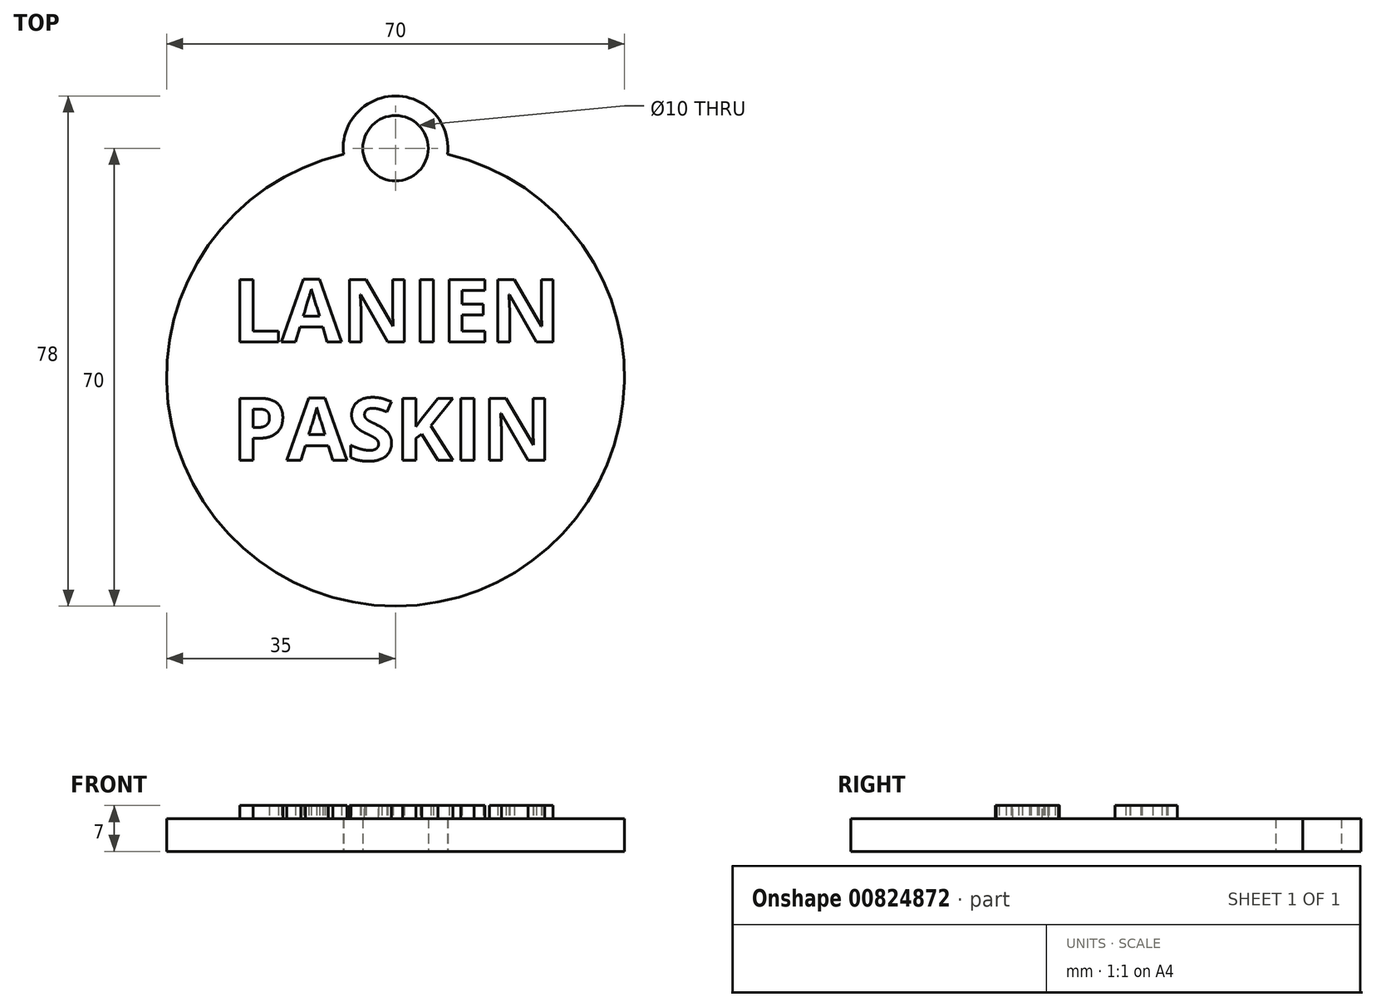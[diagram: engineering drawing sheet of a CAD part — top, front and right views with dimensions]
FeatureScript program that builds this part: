
annotation { "Feature Type Name" : "Feature", "Feature Type Description" : "" }
export const myFeature = defineFeature(function(context is Context, id is Id, definition is map)
    precondition{}
    {
        {
            var Q0;
            Q0=qCreatedBy(makeId("Top.planeOp"),FACE);
            var sketch = newSketch(context, id + "F0", { "sketchPlane" : qUnion([Q0])});
            skCircle(sketch, "E0", {"center": v(-60, 0) * mm, "radius": 35 * mm});
            skText(sketch, "E1", { "text": "LANIEN \nPASKIN", "fontName": "OpenSans-Bold.ttf"});
            skCircle(sketch, "E2", {"center": v(-60, 35) * mm, "radius": 5 * mm});
            skCircle(sketch, "E3.0", {"center": v(-60, 35) * mm, "radius": 8 * mm});
            skText(sketch, "E4", { "text": "SULO\nKUSI\n", "fontName": "OpenSans-Bold.ttf"});
            skCircle(sketch, "E5", {"center": v(60, 35) * mm, "radius": 5 * mm});
            skCircle(sketch, "E6.0", {"center": v(60, 35) * mm, "radius": 8 * mm});
            skCircle(sketch, "E7", {"center": v(60, 0) * mm, "radius": 35 * mm});
            const initialGuessF0  = {"E1": [-0.085, 0.0054, 1, 0, 0.0096], "E4": [0.035, 0.00554, 1, 0, 0.01346]};
            skSetInitialGuess(sketch, initialGuessF0);
            skSolve(sketch);
        }
        {
            var Q0;
            Q0=makeQuery(id+"F0.imprint","IMPRINT",FACE,{"disambiguationData":[TD([[makeQuery(id+"F0.imprint","IMPRINT",EDGE,{"derivedFrom":sQuery(id+"F0.wireOp",EDGE,"E1.sketch_text.stroke-0")}),1.0]])]});
            var Q1;
            Q1=makeQuery(id+"F0.imprint","IMPRINT",FACE,{"disambiguationData":[TD([[makeQuery(id+"F0.imprint","IMPRINT",EDGE,{"derivedFrom":sQuery(id+"F0.wireOp",EDGE,"E1.sketch_text.stroke-14")}),1.0]])]});
            var Q2;
            Q2=makeQuery(id+"F0.imprint","IMPRINT",FACE,{"disambiguationData":[TD([[makeQuery(id+"F0.imprint","IMPRINT",EDGE,{"derivedFrom":sQuery(id+"F0.wireOp",EDGE,"E1.sketch_text.stroke-86")}),1.0]])]});
            var Q3;
            Q3=makeQuery(id+"F0.imprint","IMPRINT",FACE,{"disambiguationData":[TD([[makeQuery(id+"F0.imprint","IMPRINT",EDGE,{"derivedFrom":sQuery(id+"F0.wireOp",EDGE,"E1.sketch_text.stroke-62")}),1.0]])]});
            var Q4;
            {var subQ0=sQuery(id+"F0.wireOp",EDGE,"E3.0");var subQ1=sQuery(id+"F0.wireOp",EDGE,"E0");var subQ2=makeQuery(id+"F0.imprint","INTERSECT",VERTEX,{"disambiguationData":[OD(0.0)],"derivedFrom":[subQ1,subQ0]});Q4=makeQuery(id+"F0.imprint","IMPRINT",FACE,{"disambiguationData":[TD([[makeQuery(id+"F0.imprint","IMPRINT",EDGE,{"disambiguationData":[TD([[subQ2,-1.0]])],"derivedFrom":subQ1}),1.0]])]});}
            var Q5;
            {var subQ0=sQuery(id+"F0.wireOp",EDGE,"E3.0");var subQ1=sQuery(id+"F0.wireOp",EDGE,"E0");var subQ2=makeQuery(id+"F0.imprint","INTERSECT",VERTEX,{"disambiguationData":[OD(0.0)],"derivedFrom":[subQ1,subQ0]});Q5=makeQuery(id+"F0.imprint","IMPRINT",FACE,{"disambiguationData":[TD([[makeQuery(id+"F0.imprint","IMPRINT",EDGE,{"disambiguationData":[TD([[subQ2,-1.0]])],"derivedFrom":subQ1}),-1.0]])]});}
            extrude(context, id + "F1", {"entities" : qUnion([Q0, Q1, Q2, Q3, Q4, Q5]), "depth" : 5 * mm, "offsetDistance" : 25 * mm});
        }
        {
            var Q0;
            Q0=makeQuery(id+"F0.imprint","IMPRINT",FACE,{"disambiguationData":[TD([[makeQuery(id+"F0.imprint","IMPRINT",EDGE,{"derivedFrom":sQuery(id+"F0.wireOp",EDGE,"E1.sketch_text.stroke-36")}),-1.0]])]});
            var Q1;
            Q1=makeQuery(id+"F0.imprint","IMPRINT",FACE,{"disambiguationData":[TD([[makeQuery(id+"F0.imprint","IMPRINT",EDGE,{"derivedFrom":sQuery(id+"F0.wireOp",EDGE,"E1.sketch_text.stroke-48")}),-1.0]])]});
            var Q2;
            Q2=makeQuery(id+"F0.imprint","IMPRINT",FACE,{"disambiguationData":[TD([[makeQuery(id+"F0.imprint","IMPRINT",EDGE,{"derivedFrom":sQuery(id+"F0.wireOp",EDGE,"E1.sketch_text.stroke-135")}),-1.0]])]});
            var Q3;
            Q3=makeQuery(id+"F0.imprint","IMPRINT",FACE,{"disambiguationData":[TD([[makeQuery(id+"F0.imprint","IMPRINT",EDGE,{"derivedFrom":sQuery(id+"F0.wireOp",EDGE,"E1.sketch_text.stroke-131")}),-1.0]])]});
            var Q4;
            Q4=makeQuery(id+"F0.imprint","IMPRINT",FACE,{"disambiguationData":[TD([[makeQuery(id+"F0.imprint","IMPRINT",EDGE,{"derivedFrom":sQuery(id+"F0.wireOp",EDGE,"E1.sketch_text.stroke-118")}),-1.0]])]});
            var Q5;
            Q5=makeQuery(id+"F0.imprint","IMPRINT",FACE,{"disambiguationData":[TD([[makeQuery(id+"F0.imprint","IMPRINT",EDGE,{"derivedFrom":sQuery(id+"F0.wireOp",EDGE,"E1.sketch_text.stroke-90")}),-1.0]])]});
            var Q6;
            Q6=makeQuery(id+"F0.imprint","IMPRINT",FACE,{"disambiguationData":[TD([[makeQuery(id+"F0.imprint","IMPRINT",EDGE,{"derivedFrom":sQuery(id+"F0.wireOp",EDGE,"E1.sketch_text.stroke-78")}),-1.0]])]});
            var Q7;
            Q7=makeQuery(id+"F0.imprint","IMPRINT",FACE,{"disambiguationData":[TD([[makeQuery(id+"F0.imprint","IMPRINT",EDGE,{"derivedFrom":sQuery(id+"F0.wireOp",EDGE,"E1.sketch_text.stroke-62")}),-1.0]])]});
            var Q8;
            Q8=makeQuery(id+"F0.imprint","IMPRINT",FACE,{"disambiguationData":[TD([[makeQuery(id+"F0.imprint","IMPRINT",EDGE,{"derivedFrom":sQuery(id+"F0.wireOp",EDGE,"E1.sketch_text.stroke-32")}),-1.0]])]});
            var Q9;
            Q9=makeQuery(id+"F0.imprint","IMPRINT",FACE,{"disambiguationData":[TD([[makeQuery(id+"F0.imprint","IMPRINT",EDGE,{"derivedFrom":sQuery(id+"F0.wireOp",EDGE,"E1.sketch_text.stroke-18")}),-1.0]])]});
            var Q10;
            Q10=makeQuery(id+"F0.imprint","IMPRINT",FACE,{"disambiguationData":[TD([[makeQuery(id+"F0.imprint","IMPRINT",EDGE,{"derivedFrom":sQuery(id+"F0.wireOp",EDGE,"E1.sketch_text.stroke-6")}),-1.0]])]});
            var Q11;
            Q11=makeQuery(id+"F0.imprint","IMPRINT",FACE,{"disambiguationData":[TD([[makeQuery(id+"F0.imprint","IMPRINT",EDGE,{"derivedFrom":sQuery(id+"F0.wireOp",EDGE,"E1.sketch_text.stroke-0")}),-1.0]])]});
            extrude(context, id + "F2", {"entities" : qUnion([Q0, Q1, Q2, Q3, Q4, Q5, Q6, Q7, Q8, Q9, Q10, Q11]), "operationType" : NewBodyOperationType.ADD, "depth" : 7 * mm, "offsetDistance" : 25 * mm});
        }
    });
